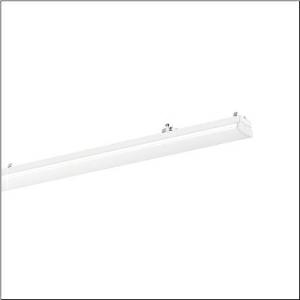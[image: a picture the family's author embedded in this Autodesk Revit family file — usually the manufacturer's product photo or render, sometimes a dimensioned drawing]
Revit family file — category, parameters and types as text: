
# Revit family: licross_11_recessed_opal_ho_51tl1ddn46xm
name_source: partatom
category: Lighting Fixtures
units: mm (PartAtom-declared; Revit-internal decimal feet)

## family parameters
Cut with Voids When Loaded = No
Host = Face
Light Source = No
Part Type = Normal
Room Calculation Point = No
Round Connector Dimension = Use Diameter
Shared = No

## types (1)
- --- (1 x LED, 6320 lm, 33.5 W, 4000K)
    Apparent Load = 34 VA
    CIE Flux Codes = 44 73 91 87 100
    Color Rendering = 80
    Color Temperature = 4000K
    Default Elevation = 1800 mm
    Description = Licross 11 recessed opal HO, luminaire insert, of sheet steel, coil coated, white, length: 1.500mm, width: 76mm, height: 87mm, LED rated luminous flux: 6.320lm, light colour: 840, SDCM (Standard Deviation of Colour Matching)MacAdam ≤ 2 SDCM (initial), control gear: DALI 2, with plug, 5-pole, with phase selection, mains connection: 220..240V, AC, 50/60Hz, rated input power: 34W, internal wiring halogen-free, primary optical cover: cover, of PMMA, light emission: direct with ceiling illumination distribution, primary light characteristic: symmetric, protection rating (complete): IP40, insulation class (complete): insulation class I (protective earthing), certification: CE, ENEC, VDE, UKCA, protection symbol: D if used in an environment without relevant dust loads with corresponding accessories, impact resistance: IK06, permissible ambient temperature for indoor applications: -25..+45°C, corresponds to IFS (International Featured Standards) requirements for safety and quality in the food industry, reducing of maximum allowable ambient temperature of 5°C with ceiling mounting, LABS conformity tested according to VDMA 24364:2018-05, The light source and the operating device comply with the requirements of the Ecodesign Regulation (EU) 2019/2020 and are replaceable in accordance with this regulation, packaging unit: 1 piece
    Height = 83 mm
    Lamp = 1 x LED
    Lamp Light Flux = 6320 lm
    Lamp Power = 33.5 W
    Lamp count = 1
    Length = 1500 mm
    Luminous efficacy = 189 lm/W
    Manufacturer = Siteco
    ModVariant = No
    Model = 51TL1DDN46XM
    Mounting Place = Ceiling
    Mounting Type = Pendant
    Number of Poles = 1
    OnlyDefault = Yes
    Power Factor = 1
    Product Name = Licross 11 recessed opal HO
    Product group = luminaire insert | ceiling pendant
    ProductGroupID = 901
    Protection Class = Protection class I
    Protection Degree = IP 40
    RLX_Detail_Level = 1
    RLX_Emergency_Light_Flux = 0 lm
    RLX_Emergency_Type = 0
    RLX_Emergency_Type_DB = No
    RlxData = <blob elided: 27121 chars, md5=0cb6224d>
    Socket = socket
    Standby Power = 0 W
    System Light Flux = 6320 lm
    System Power = 34 W
    Type Comments = factory setting: luminous flux: 100 % | dim-lin: 254 | 232 mA
    Type Image = l_1313666.jpg
    URL = http://relux.com
    VarID = @adj_083849
    Voltage = 0 V
    Weight = 0.00 kg
    Width = 76 mm

## geometry (parser evidence)
native form markers: Blend x4, Sweep x14
no freeform markers — native parametric forms only
